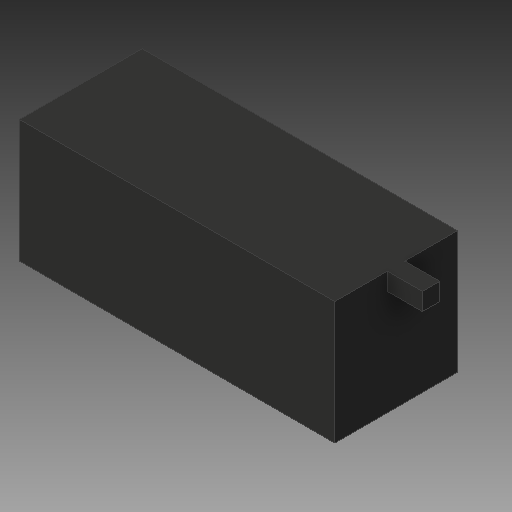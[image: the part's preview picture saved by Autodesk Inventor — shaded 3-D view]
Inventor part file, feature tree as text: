
AUTODESK INVENTOR PART (.ipt)
format: ipt  version: 2019 (Build 230136000, 136)  size: 97,280 bytes
history: native  units: in
note: dims shown in document units (in); Inventor stores cm internally (conversion verified against a paired STEP export)
features: extrude x2, sketch x2
ambient origin geometry x8: Origin, YZ Plane, XZ Plane, XY Plane, X Axis, Y Axis, Z Axis, Center Point
bodies: Solid1 (feature_tree)
feature tree (4):
  extrude  "Extrusion1"  Depth=1.75in
  extrude  "Extrusion2"  Depth=0.75in
  sketch  "Sketch1"  dims[d0=4.5in d1=1.75in]
  sketch  "Sketch2"  dims[d2=1.75in d3=0.0in d4=0.75in d5=0.75in d6=0.25in d7=0.25in d8=0.5in d9=0.0in]
